# Revit family: Doors-Sliding_WON-DOOR_Fireguard-FG-Slim_Rods
name_source: partatom
category: Doors
units: mm (PartAtom-declared; Revit-internal decimal feet)

## family parameters
Always vertical = Yes
Cut with Voids When Loaded = No
Host = Wall
OmniClass Number = 23.17.11.31
Room Calculation Point = No
Shared = No

## types (2) — shared parameters
Description = The development of the accordion-type, horizontal sliding fire door– invented by Won-Door Corporation – has had a profound influence on the model code requirements that regulate their use. They may replace traditional solutions in virtually any means of egress. The Won-Door FireGuard Slim door is specifically designed for straight, single-parting applications that are 7' or 8' in height and up to 9' wide clear opening.
Door Finish = Won-Door-Metal-Platinum
Manufacturer = Won-Door Corporation
Model = Fireguard FG Slim
Offset for Backing Depth = 0' - 6 1/8"
Offset for Backing Width = 0' - 3 1/8"
Offset for Stack Depth = 0' - 4 7/8"
Pocket Thickness = 2' - 3 3/4"
Product Page URL = https://wondoor.concora.com
Product data url = https://bimobject.com
Thickness = 1' - 6"
URL = https://www.wondoor.com
Version = 1
Wall Closure = By host

## per-type parameters (varying)
| type | Height |
| Height 7'-0" | 7' - 0" |
| Height 8'-0" | 8' - 0" |

## geometry (parser evidence)
native form markers: Sweep x10
no freeform markers — native parametric forms only
